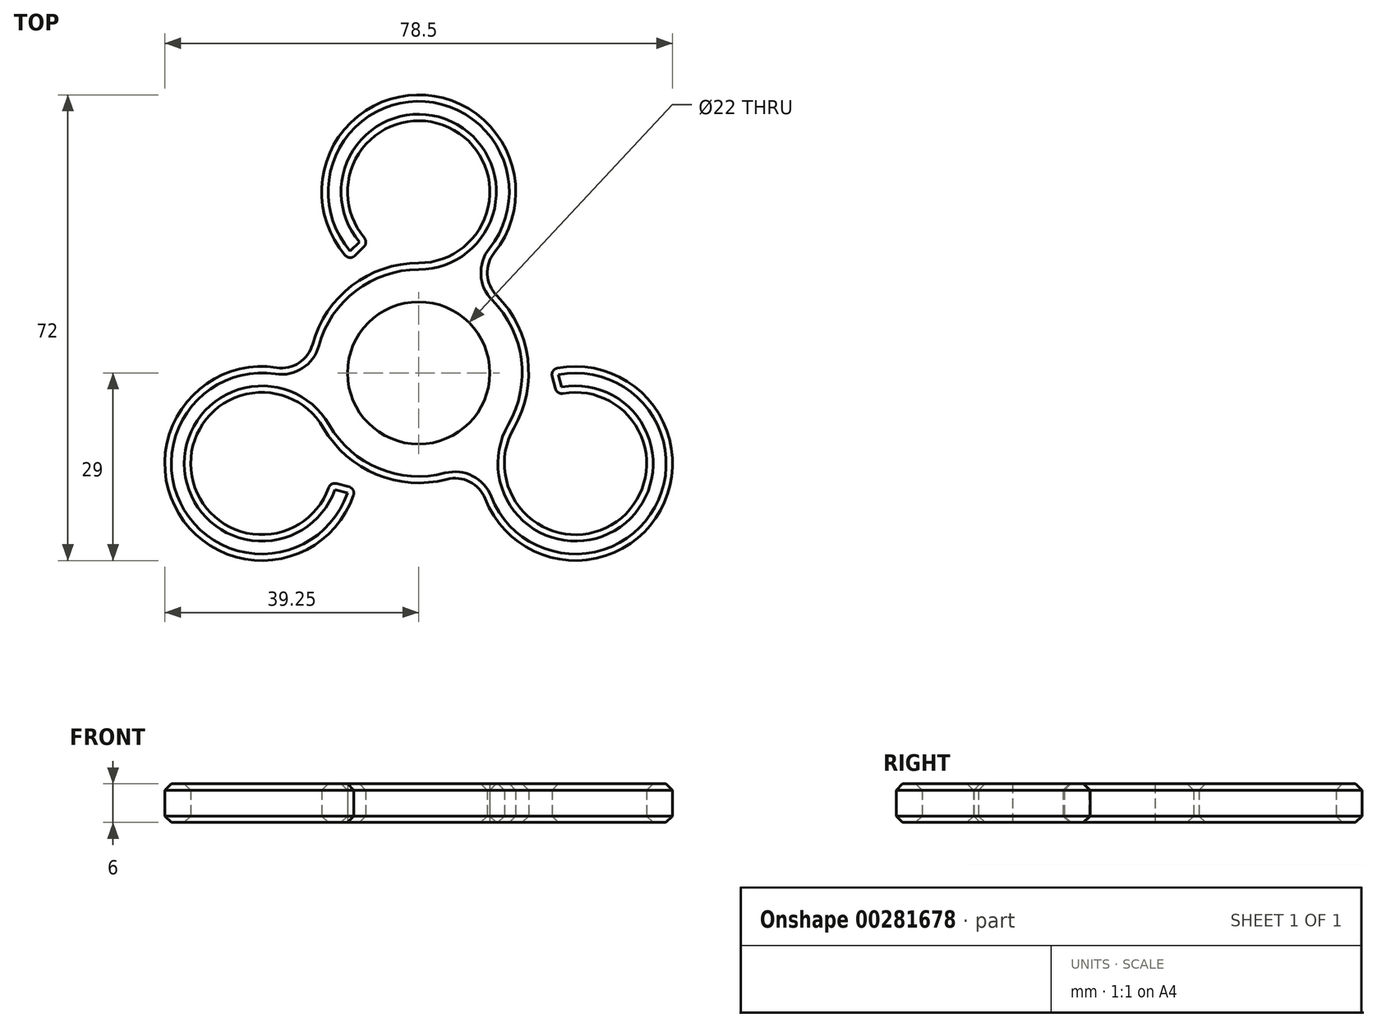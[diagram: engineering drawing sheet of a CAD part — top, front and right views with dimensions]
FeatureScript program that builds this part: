
annotation { "Feature Type Name" : "Feature", "Feature Type Description" : "" }
export const myFeature = defineFeature(function(context is Context, id is Id, definition is map)
    precondition{}
    {
        {
            var Q0;
            Q0=qCreatedBy(makeId("Top.planeOp"),FACE);
            var sketch = newSketch(context, id + "F0", { "sketchPlane" : qUnion([Q0])});
            skCircle(sketch, "E0", {"center": v(0, 0) * mm, "radius": 11 * mm});
            skArc(sketch, "E1", {"start": v(0, 17) * mm, "mid": v(-10.32, 13.5) * mm, "end": v(-16.4, 4.46) * mm});
            skArc(sketch, "E2", {"start": v(0, 17) * mm, "mid": v(4.63, 37.98) * mm, "end": v(-8.4, 20.9) * mm});
            skLineSegment(sketch, "E3", {"start": v(-8.46, 19.54) * mm, "end": v(-9.87, 18.13) * mm});
            skArc(sketch, "E4", {"start": v(11.7, 18.63) * mm, "mid": v(-0.3, 43) * mm, "end": v(-11.34, 18.18) * mm});
            skPoint(sketch, "E5.visualSharp", {"position": v(-7.78, 20.22) * mm});
            skArc(sketch, "E5.filletArc", {"start": v(-8.46, 19.54) * mm, "mid": v(-8.16, 20.2) * mm, "end": v(-8.4, 20.9) * mm});
            skPoint(sketch, "E6.visualSharp", {"position": v(-10.6, 17.4) * mm});
            skArc(sketch, "E6.filletArc", {"start": v(-11.34, 18.18) * mm, "mid": v(-10.62, 17.83) * mm, "end": v(-9.87, 18.13) * mm});
            skPoint(sketch, "E7.visualSharp", {"position": v(7.73, 15.14) * mm});
            skArc(sketch, "E7.filletArc", {"start": v(11.7, 18.63) * mm, "mid": v(10.62, 15.23) * mm, "end": v(12.06, 11.98) * mm});
            skPoint(sketch, "E8.1.0", {"position": v(-13.62, -16.85) * mm});
            skArc(sketch, "E8.1.1", {"start": v(-21.98, 0.83) * mm, "mid": v(-18.5, 1.58) * mm, "end": v(-16.4, 4.46) * mm});
            skArc(sketch, "E8.1.2", {"start": v(-21.98, 0.83) * mm, "mid": v(-37.1, -21.75) * mm, "end": v(-10.07, -18.9) * mm});
            skArc(sketch, "E8.1.3", {"start": v(-14.72, -8.5) * mm, "mid": v(-35.2, -14.98) * mm, "end": v(-13.9, -17.72) * mm});
            skPoint(sketch, "E8.1.4", {"position": v(-9.76, -17.88) * mm});
            skPoint(sketch, "E8.1.5", {"position": v(-16.98, -0.88) * mm});
            skLineSegment(sketch, "E8.1.6", {"start": v(-12.7, -17.1) * mm, "end": v(-10.76, -17.61) * mm});
            skArc(sketch, "E8.1.7", {"start": v(-10.07, -18.9) * mm, "mid": v(-10.14, -18.11) * mm, "end": v(-10.76, -17.61) * mm});
            skArc(sketch, "E8.1.8", {"start": v(-12.7, -17.1) * mm, "mid": v(-13.42, -17.17) * mm, "end": v(-13.9, -17.72) * mm});
            skPoint(sketch, "E8.2.0", {"position": v(21.4, -3.37) * mm});
            skArc(sketch, "E8.2.1", {"start": v(10.28, -19.45) * mm, "mid": v(7.88, -16.81) * mm, "end": v(4.34, -16.44) * mm});
            skArc(sketch, "E8.2.2", {"start": v(10.28, -19.45) * mm, "mid": v(37.38, -21.25) * mm, "end": v(21.41, 0.73) * mm});
            skArc(sketch, "E8.2.3", {"start": v(14.72, -8.5) * mm, "mid": v(30.58, -23) * mm, "end": v(22.3, -3.17) * mm});
            skPoint(sketch, "E8.2.4", {"position": v(20.37, 0.49) * mm});
            skPoint(sketch, "E8.2.5", {"position": v(9.25, -14.26) * mm});
            skLineSegment(sketch, "E8.2.6", {"start": v(21.15, -2.45) * mm, "end": v(20.63, -0.51) * mm});
            skArc(sketch, "E8.2.7", {"start": v(21.41, 0.73) * mm, "mid": v(20.75, 0.28) * mm, "end": v(20.63, -0.51) * mm});
            skArc(sketch, "E8.2.8", {"start": v(21.15, -2.45) * mm, "mid": v(21.58, -3.03) * mm, "end": v(22.3, -3.17) * mm});
            skArc(sketch, "E9.trimOffspring", {"start": v(-14.72, -8.5) * mm, "mid": v(-6.53, -15.7) * mm, "end": v(4.34, -16.44) * mm});
            skArc(sketch, "E10.trimOffspring", {"start": v(14.72, -8.5) * mm, "mid": v(16.86, 2.19) * mm, "end": v(12.06, 11.98) * mm});
            skSolve(sketch);
        }
        {
            var Q0;
            Q0=makeQuery(id+"F0.imprint","IMPRINT",FACE,{"disambiguationData":[TD([[makeQuery(id+"F0.imprint","IMPRINT",EDGE,{"derivedFrom":sQuery(id+"F0.wireOp",EDGE,"E0")}),-1.0]])]});
            extrude(context, id + "F1", {"entities" : qUnion([Q0]), "depth" : 6 * mm});
        }
        {
            var Q0;
            Q0=makeQuery(id+"F1.opExtrude","CAP_EDGE",EDGE,{"disambiguationData":[OSD([sQuery(id+"F0.wireOp",EDGE,"E8.1.2")])],"isStart":false});
            var Q1;
            Q1=makeQuery(id+"F1.opExtrude","CAP_EDGE",EDGE,{"disambiguationData":[OSD([sQuery(id+"F0.wireOp",EDGE,"E8.2.2")])],"isStart":true});
            chamfer(context, id + "F2", {"entities" : qUnion([Q0, Q1]), "width" : 1 * mm, "tangentPropagation" : true});
        }
    });
